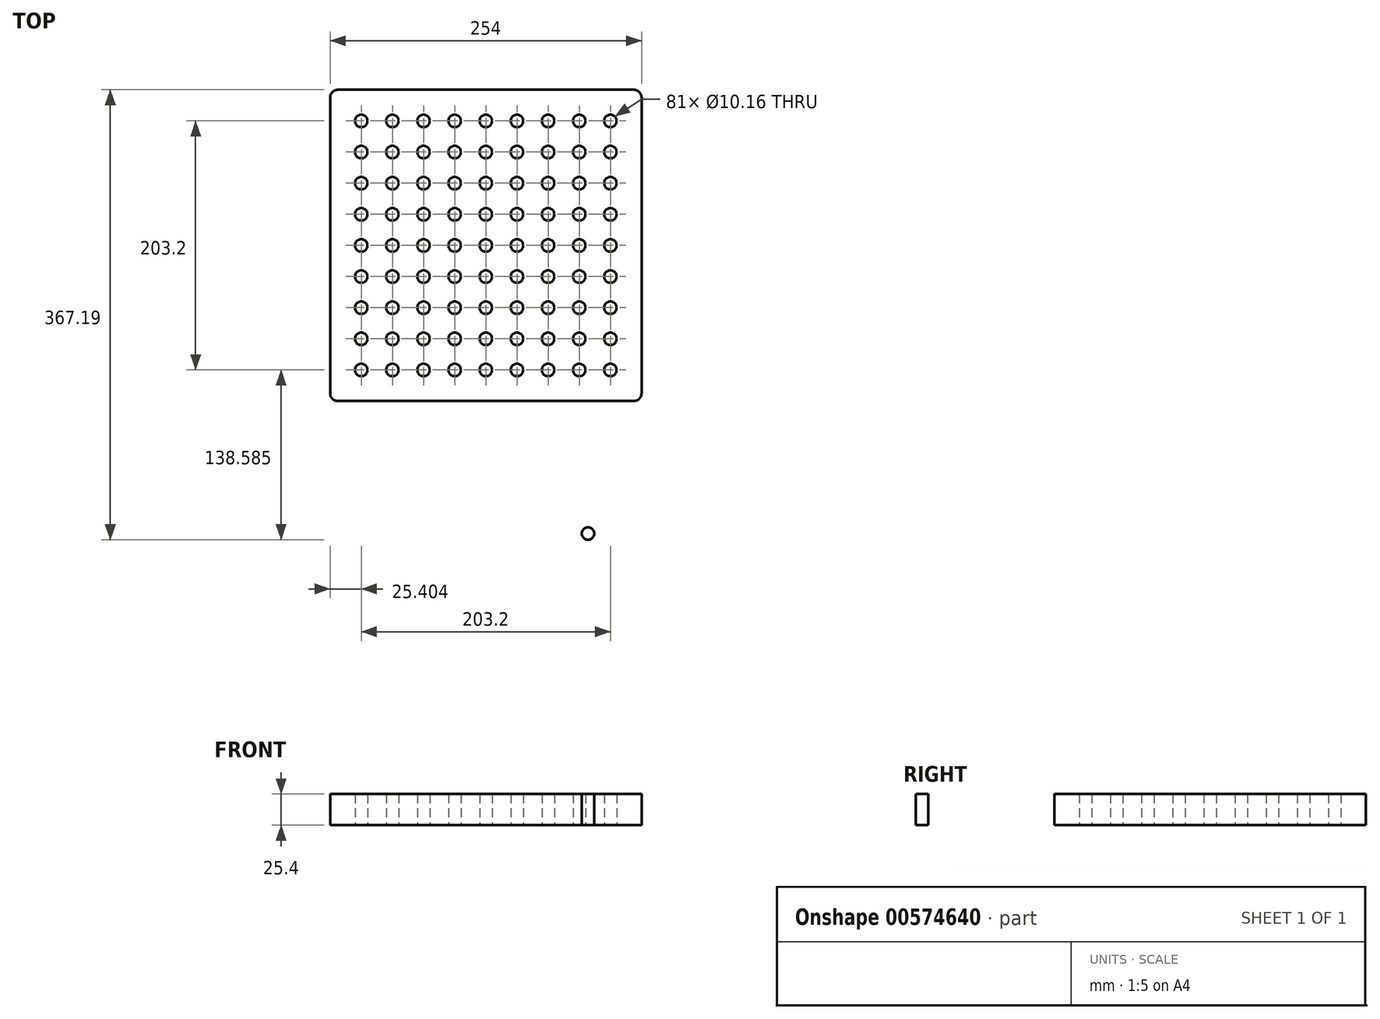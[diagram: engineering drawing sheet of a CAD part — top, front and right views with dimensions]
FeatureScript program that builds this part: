
annotation { "Feature Type Name" : "Feature", "Feature Type Description" : "" }
export const myFeature = defineFeature(function(context is Context, id is Id, definition is map)
    precondition{}
    {
        {
            var Q0;
            Q0=qCreatedBy(makeId("Top.planeOp"),FACE);
            var sketch = newSketch(context, id + "F0", { "sketchPlane" : qUnion([Q0])});
            skLineSegment(sketch, "E0", {"start": v(58.7, 104.27) * mm, "end": v(-61.95, 104.27) * mm});
            skLineSegment(sketch, "E1", {"start": v(-68.3, 97.92) * mm, "end": v(-68.3, -22.73) * mm});
            skCircle(sketch, "E2", {"center": v(58.7, -22.73) * mm, "radius": 5.08 * mm});
            skPoint(sketch, "E3.visualSharp", {"position": v(-68.3, 104.27) * mm});
            skArc(sketch, "E3.filletArc", {"start": v(-61.95, 104.27) * mm, "mid": v(-66.44, 102.4) * mm, "end": v(-68.3, 97.92) * mm});
            skCircle(sketch, "E4.0.1.0", {"center": v(58.7, 2.67) * mm, "radius": 5.08 * mm});
            skCircle(sketch, "E4.0.2.0", {"center": v(58.7, 28.07) * mm, "radius": 5.08 * mm});
            skCircle(sketch, "E4.0.3.0", {"center": v(58.7, 53.47) * mm, "radius": 5.08 * mm});
            skCircle(sketch, "E4.0.4.0", {"center": v(58.7, 78.87) * mm, "radius": 5.08 * mm});
            skCircle(sketch, "E4.1.0.0", {"center": v(33.3, -22.73) * mm, "radius": 5.08 * mm});
            skCircle(sketch, "E4.1.1.0", {"center": v(33.3, 2.67) * mm, "radius": 5.08 * mm});
            skCircle(sketch, "E4.1.2.0", {"center": v(33.3, 28.07) * mm, "radius": 5.08 * mm});
            skCircle(sketch, "E4.1.3.0", {"center": v(33.3, 53.47) * mm, "radius": 5.08 * mm});
            skCircle(sketch, "E4.1.4.0", {"center": v(33.3, 78.87) * mm, "radius": 5.08 * mm});
            skCircle(sketch, "E4.2.0.0", {"center": v(7.9, -22.73) * mm, "radius": 5.08 * mm});
            skCircle(sketch, "E4.2.1.0", {"center": v(7.9, 2.67) * mm, "radius": 5.08 * mm});
            skCircle(sketch, "E4.2.2.0", {"center": v(7.9, 28.07) * mm, "radius": 5.08 * mm});
            skCircle(sketch, "E4.2.3.0", {"center": v(7.9, 53.47) * mm, "radius": 5.08 * mm});
            skCircle(sketch, "E4.2.4.0", {"center": v(7.9, 78.87) * mm, "radius": 5.08 * mm});
            skCircle(sketch, "E4.3.0.0", {"center": v(-17.5, -22.73) * mm, "radius": 5.08 * mm});
            skCircle(sketch, "E4.3.1.0", {"center": v(-17.5, 2.67) * mm, "radius": 5.08 * mm});
            skCircle(sketch, "E4.3.2.0", {"center": v(-17.5, 28.07) * mm, "radius": 5.08 * mm});
            skCircle(sketch, "E4.3.3.0", {"center": v(-17.5, 53.47) * mm, "radius": 5.08 * mm});
            skCircle(sketch, "E4.3.4.0", {"center": v(-17.5, 78.87) * mm, "radius": 5.08 * mm});
            skCircle(sketch, "E4.4.0.0", {"center": v(-42.9, -22.73) * mm, "radius": 5.08 * mm});
            skCircle(sketch, "E4.4.1.0", {"center": v(-42.9, 2.67) * mm, "radius": 5.08 * mm});
            skCircle(sketch, "E4.4.2.0", {"center": v(-42.9, 28.07) * mm, "radius": 5.08 * mm});
            skCircle(sketch, "E4.4.3.0", {"center": v(-42.9, 53.47) * mm, "radius": 5.08 * mm});
            skCircle(sketch, "E4.4.4.0", {"center": v(-42.9, 78.87) * mm, "radius": 5.08 * mm});
            skLineSegment(sketch, "E4.direction1", {"start": v(58.7, -22.73) * mm, "end": v(33.3, -22.73) * mm, "construction": true});
            skLineSegment(sketch, "E4.direction2", {"start": v(58.7, -22.73) * mm, "end": v(58.7, 2.67) * mm, "construction": true});
            skArc(sketch, "E5.MirrorCS", {"start": v(-61.95, -149.73) * mm, "mid": v(-66.44, -147.88) * mm, "end": v(-68.3, -143.38) * mm});
            skCircle(sketch, "E6.MirrorC", {"center": v(7.9, -98.93) * mm, "radius": 5.08 * mm});
            skLineSegment(sketch, "E7.MirrorCS", {"start": v(58.7, -22.73) * mm, "end": v(58.7, -48.13) * mm, "construction": true});
            skCircle(sketch, "E8.MirrorC", {"center": v(-17.5, -73.53) * mm, "radius": 5.08 * mm});
            skCircle(sketch, "E9.MirrorC", {"center": v(7.9, -73.53) * mm, "radius": 5.08 * mm});
            skCircle(sketch, "E10.MirrorC", {"center": v(-17.5, -48.13) * mm, "radius": 5.08 * mm});
            skCircle(sketch, "E11.MirrorC", {"center": v(-17.5, -124.33) * mm, "radius": 5.08 * mm});
            skCircle(sketch, "E12.MirrorC", {"center": v(-42.9, -98.93) * mm, "radius": 5.08 * mm});
            skCircle(sketch, "E13.MirrorC", {"center": v(7.9, -48.13) * mm, "radius": 5.08 * mm});
            skCircle(sketch, "E14.MirrorC", {"center": v(-42.9, -124.33) * mm, "radius": 5.08 * mm});
            skCircle(sketch, "E15.MirrorC", {"center": v(-17.5, -98.93) * mm, "radius": 5.08 * mm});
            skCircle(sketch, "E16.MirrorC", {"center": v(-42.9, -73.53) * mm, "radius": 5.08 * mm});
            skCircle(sketch, "E17.MirrorC", {"center": v(33.3, -73.53) * mm, "radius": 5.08 * mm});
            skCircle(sketch, "E18.MirrorC", {"center": v(33.3, -48.13) * mm, "radius": 5.08 * mm});
            skCircle(sketch, "E19.MirrorC", {"center": v(58.7, -124.33) * mm, "radius": 5.08 * mm});
            skCircle(sketch, "E20.MirrorC", {"center": v(58.7, -98.93) * mm, "radius": 5.08 * mm});
            skCircle(sketch, "E21.MirrorC", {"center": v(58.7, -73.53) * mm, "radius": 5.08 * mm});
            skCircle(sketch, "E22.MirrorC", {"center": v(58.7, -48.13) * mm, "radius": 5.08 * mm});
            skLineSegment(sketch, "E23.MirrorCS", {"start": v(-68.3, -143.38) * mm, "end": v(-68.3, -22.73) * mm});
            skLineSegment(sketch, "E24.MirrorCS", {"start": v(58.7, -149.73) * mm, "end": v(-61.95, -149.73) * mm});
            skPoint(sketch, "E25.MirrorP", {"position": v(-68.3, -149.73) * mm});
            skCircle(sketch, "E26.MirrorC", {"center": v(33.3, -98.93) * mm, "radius": 5.08 * mm});
            skCircle(sketch, "E27.MirrorC", {"center": v(-42.9, -48.13) * mm, "radius": 5.08 * mm});
            skCircle(sketch, "E28.MirrorC", {"center": v(7.9, -124.33) * mm, "radius": 5.08 * mm});
            skCircle(sketch, "E29.MirrorC", {"center": v(33.3, -124.33) * mm, "radius": 5.08 * mm});
            skArc(sketch, "E30.MirrorCS", {"start": v(179.35, -149.73) * mm, "mid": v(183.84, -147.88) * mm, "end": v(185.7, -143.38) * mm});
            skArc(sketch, "E31.MirrorCS", {"start": v(179.35, 104.27) * mm, "mid": v(183.84, 102.4) * mm, "end": v(185.7, 97.92) * mm});
            skPoint(sketch, "E32.MirrorP", {"position": v(185.7, 104.27) * mm});
            skCircle(sketch, "E33.MirrorC", {"center": v(109.5, 53.47) * mm, "radius": 5.08 * mm});
            skCircle(sketch, "E34.MirrorC", {"center": v(160.3, -22.73) * mm, "radius": 5.08 * mm});
            skCircle(sketch, "E35.MirrorC", {"center": v(160.3, -124.33) * mm, "radius": 5.08 * mm});
            skCircle(sketch, "E36.MirrorC", {"center": v(109.5, -98.93) * mm, "radius": 5.08 * mm});
            skCircle(sketch, "E37.MirrorC", {"center": v(109.5, 28.07) * mm, "radius": 5.08 * mm});
            skCircle(sketch, "E38.MirrorC", {"center": v(134.9, 78.87) * mm, "radius": 5.08 * mm});
            skCircle(sketch, "E39.MirrorC", {"center": v(109.5, -48.13) * mm, "radius": 5.08 * mm});
            skCircle(sketch, "E40.MirrorC", {"center": v(84.1, -124.33) * mm, "radius": 5.08 * mm});
            skCircle(sketch, "E41.MirrorC", {"center": v(109.5, 2.67) * mm, "radius": 5.08 * mm});
            skCircle(sketch, "E42.MirrorC", {"center": v(134.9, 53.47) * mm, "radius": 5.08 * mm});
            skCircle(sketch, "E43.MirrorC", {"center": v(160.3, -98.93) * mm, "radius": 5.08 * mm});
            skCircle(sketch, "E44.MirrorC", {"center": v(109.5, -124.33) * mm, "radius": 5.08 * mm});
            skCircle(sketch, "E45.MirrorC", {"center": v(84.1, 28.07) * mm, "radius": 5.08 * mm});
            skCircle(sketch, "E46.MirrorC", {"center": v(84.1, 2.67) * mm, "radius": 5.08 * mm});
            skCircle(sketch, "E47.MirrorC", {"center": v(84.1, -22.73) * mm, "radius": 5.08 * mm});
            skCircle(sketch, "E48.MirrorC", {"center": v(134.9, 28.07) * mm, "radius": 5.08 * mm});
            skCircle(sketch, "E49.MirrorC", {"center": v(134.9, -98.93) * mm, "radius": 5.08 * mm});
            skCircle(sketch, "E50.MirrorC", {"center": v(160.3, 2.67) * mm, "radius": 5.08 * mm});
            skCircle(sketch, "E51.MirrorC", {"center": v(160.3, -48.13) * mm, "radius": 5.08 * mm});
            skCircle(sketch, "E52.MirrorC", {"center": v(134.9, -124.33) * mm, "radius": 5.08 * mm});
            skCircle(sketch, "E53.MirrorC", {"center": v(109.5, 78.87) * mm, "radius": 5.08 * mm});
            skCircle(sketch, "E54.MirrorC", {"center": v(84.1, 53.47) * mm, "radius": 5.08 * mm});
            skCircle(sketch, "E55.MirrorC", {"center": v(84.1, 78.87) * mm, "radius": 5.08 * mm});
            skLineSegment(sketch, "E56.MirrorCS", {"start": v(185.7, -143.38) * mm, "end": v(185.7, -22.73) * mm});
            skCircle(sketch, "E57.MirrorC", {"center": v(134.9, -73.53) * mm, "radius": 5.08 * mm});
            skCircle(sketch, "E58.MirrorC", {"center": v(109.5, -22.73) * mm, "radius": 5.08 * mm});
            skPoint(sketch, "E59.MirrorP", {"position": v(185.7, -149.73) * mm});
            skLineSegment(sketch, "E60.MirrorCS", {"start": v(185.7, 97.92) * mm, "end": v(185.7, -22.73) * mm});
            skCircle(sketch, "E61.MirrorC", {"center": v(160.3, -73.53) * mm, "radius": 5.08 * mm});
            skCircle(sketch, "E62.MirrorC", {"center": v(160.3, 28.07) * mm, "radius": 5.08 * mm});
            skCircle(sketch, "E63.MirrorC", {"center": v(134.9, -22.73) * mm, "radius": 5.08 * mm});
            skCircle(sketch, "E64.MirrorC", {"center": v(84.1, -48.13) * mm, "radius": 5.08 * mm});
            skCircle(sketch, "E65.MirrorC", {"center": v(109.5, -73.53) * mm, "radius": 5.08 * mm});
            skCircle(sketch, "E66.MirrorC", {"center": v(160.3, 78.87) * mm, "radius": 5.08 * mm});
            skCircle(sketch, "E67.MirrorC", {"center": v(84.1, -73.53) * mm, "radius": 5.08 * mm});
            skCircle(sketch, "E68.MirrorC", {"center": v(160.3, 53.47) * mm, "radius": 5.08 * mm});
            skCircle(sketch, "E69.MirrorC", {"center": v(134.9, 2.67) * mm, "radius": 5.08 * mm});
            skCircle(sketch, "E70.MirrorC", {"center": v(84.1, -98.93) * mm, "radius": 5.08 * mm});
            skCircle(sketch, "E71.MirrorC", {"center": v(134.9, -48.13) * mm, "radius": 5.08 * mm});
            skLineSegment(sketch, "E72.MirrorCS", {"start": v(58.7, 104.27) * mm, "end": v(179.35, 104.27) * mm});
            skLineSegment(sketch, "E73.MirrorCS", {"start": v(58.7, -149.73) * mm, "end": v(179.35, -149.73) * mm});
            skCircle(sketch, "E74", {"center": v(142.05, -257.84) * mm, "radius": 5.08 * mm});
            skSolve(sketch);
        }
        {
            var Q0;
            Q0=makeQuery(id+"F0.imprint","IMPRINT",FACE,{"disambiguationData":[TD([[makeQuery(id+"F0.imprint","IMPRINT",EDGE,{"derivedFrom":sQuery(id+"F0.wireOp",EDGE,"E0")}),1.0]])]});
            extrude(context, id + "F1", {"entities" : qUnion([Q0]), "depth" : 2.54 * mm, "offsetDistance" : 25.4 * mm});
        }
        {
            var Q0;
            Q0 = qSketchRegion(id + "F0", true);
            extrude(context, id + "F2", {"entities" : qUnion([Q0]), "operationType" : NewBodyOperationType.ADD, "depth" : 25.4 * mm, "offsetDistance" : 25.4 * mm});
        }
    });
